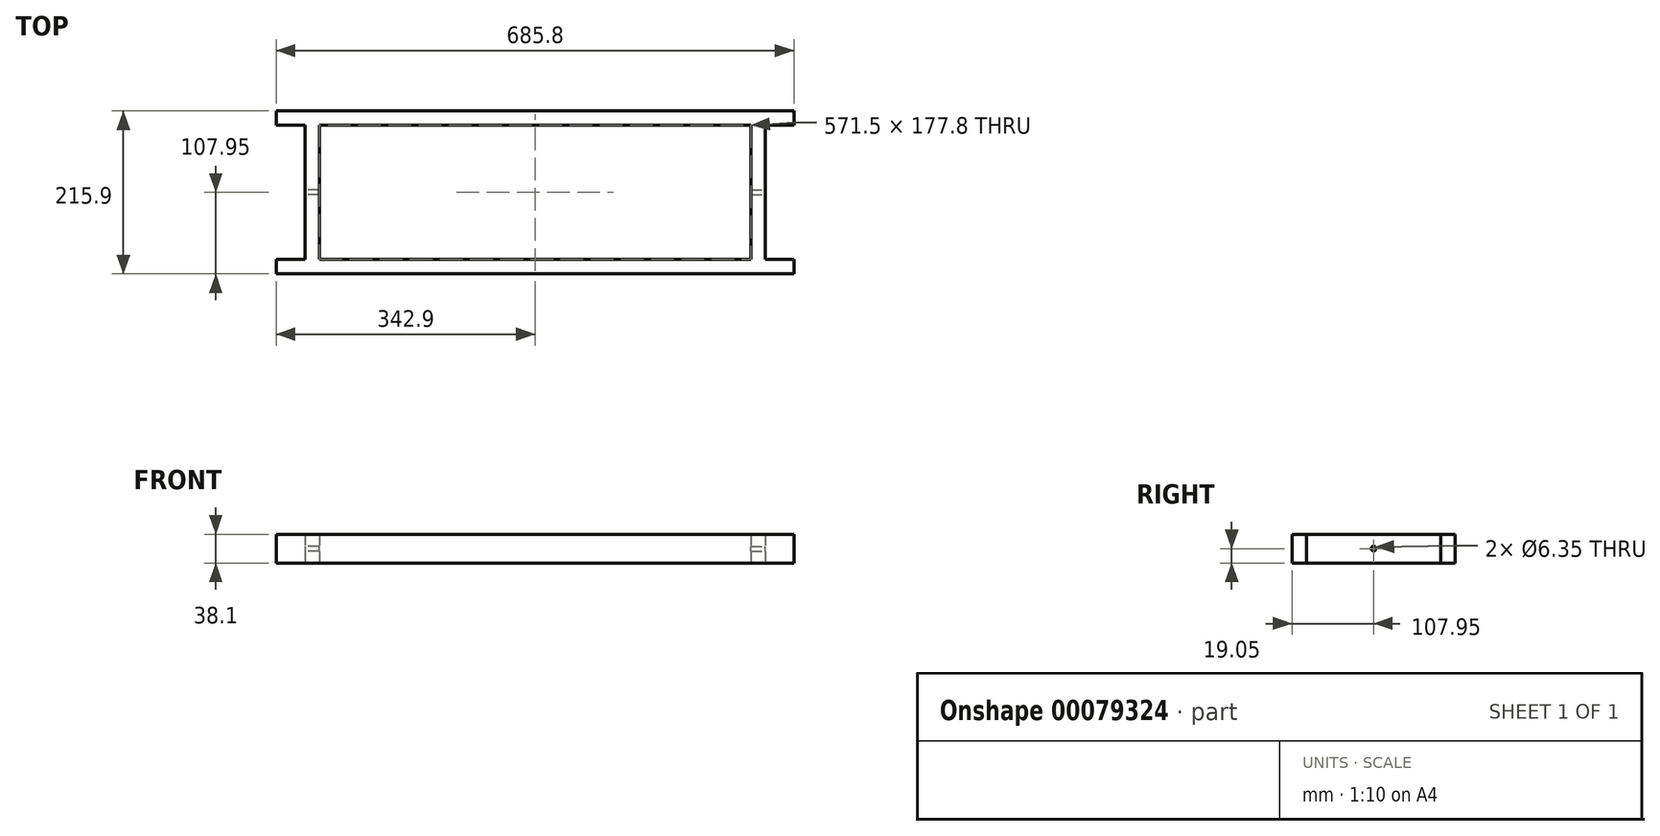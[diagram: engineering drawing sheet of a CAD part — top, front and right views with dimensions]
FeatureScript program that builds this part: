
annotation { "Feature Type Name" : "Feature", "Feature Type Description" : "" }
export const myFeature = defineFeature(function(context is Context, id is Id, definition is map)
    precondition{}
    {
        {
            var Q0;
            Q0=qCreatedBy(makeId("Top.planeOp"),FACE);
            var sketch = newSketch(context, id + "F0", { "sketchPlane" : qUnion([Q0])});
            skLineSegment(sketch, "E0.bottom", {"start": v(-342.9, 107.95) * mm, "end": v(342.9, 107.95) * mm});
            skLineSegment(sketch, "E0.top", {"start": v(-342.9, 88.9) * mm, "end": v(342.9, 88.9) * mm});
            skLineSegment(sketch, "E0.left", {"start": v(-342.9, 107.95) * mm, "end": v(-342.9, 88.9) * mm});
            skLineSegment(sketch, "E0.right", {"start": v(342.9, 107.95) * mm, "end": v(342.9, 88.9) * mm});
            skLineSegment(sketch, "E1.bottom", {"start": v(-342.9, -107.95) * mm, "end": v(342.9, -107.95) * mm});
            skLineSegment(sketch, "E1.top", {"start": v(-342.9, -88.9) * mm, "end": v(342.9, -88.9) * mm});
            skLineSegment(sketch, "E1.left", {"start": v(-342.9, -107.95) * mm, "end": v(-342.9, -88.9) * mm});
            skLineSegment(sketch, "E1.right", {"start": v(342.9, -107.95) * mm, "end": v(342.9, -88.9) * mm});
            skLineSegment(sketch, "E2.bottom", {"start": v(-304.8, 88.9) * mm, "end": v(-285.75, 88.9) * mm});
            skLineSegment(sketch, "E2.top", {"start": v(-304.8, -88.9) * mm, "end": v(-285.75, -88.9) * mm});
            skLineSegment(sketch, "E2.left", {"start": v(-304.8, 88.9) * mm, "end": v(-304.8, -88.9) * mm});
            skLineSegment(sketch, "E2.right", {"start": v(-285.75, 88.9) * mm, "end": v(-285.75, -88.9) * mm});
            skLineSegment(sketch, "E3.bottom", {"start": v(-107.95, 88.9) * mm, "end": v(-88.9, 88.9) * mm});
            skLineSegment(sketch, "E3.top", {"start": v(-107.95, -88.9) * mm, "end": v(-88.9, -88.9) * mm});
            skLineSegment(sketch, "E3.left", {"start": v(-107.95, 88.9) * mm, "end": v(-107.95, -88.9) * mm});
            skLineSegment(sketch, "E3.right", {"start": v(-88.9, 88.9) * mm, "end": v(-88.9, -88.9) * mm});
            skLineSegment(sketch, "E4.bottom", {"start": v(304.8, 88.9) * mm, "end": v(285.75, 88.9) * mm});
            skLineSegment(sketch, "E4.top", {"start": v(304.8, -88.9) * mm, "end": v(285.75, -88.9) * mm});
            skLineSegment(sketch, "E4.left", {"start": v(304.8, 88.9) * mm, "end": v(304.8, -88.9) * mm});
            skLineSegment(sketch, "E4.right", {"start": v(285.75, 88.9) * mm, "end": v(285.75, -88.9) * mm});
            skLineSegment(sketch, "E5.bottom", {"start": v(107.95, 88.9) * mm, "end": v(88.9, 88.9) * mm});
            skLineSegment(sketch, "E5.top", {"start": v(107.95, -88.9) * mm, "end": v(88.9, -88.9) * mm});
            skLineSegment(sketch, "E5.left", {"start": v(107.95, 88.9) * mm, "end": v(107.95, -88.9) * mm});
            skLineSegment(sketch, "E5.right", {"start": v(88.9, 88.9) * mm, "end": v(88.9, -88.9) * mm});
            skSolve(sketch);
        }
        {
            var Q0;
            Q0 = qSketchRegion(id + "F0", true);
            var Q1;
            Q1=makeQuery(id+"F0.imprint","IMPRINT",FACE,{"disambiguationData":[TD([[makeQuery(id+"F0.imprint","IMPRINT",EDGE,{"derivedFrom":sQuery(id+"F0.wireOp",EDGE,"E3.bottom")}),-1.0]])]});
            var Q2;
            Q2=makeQuery(id+"F0.imprint","IMPRINT",FACE,{"disambiguationData":[TD([[makeQuery(id+"F0.imprint","IMPRINT",EDGE,{"derivedFrom":sQuery(id+"F0.wireOp",EDGE,"E5.bottom")}),1.0]])]});
            extrude(context, id + "F1", {"entities" : qUnion([Q0, Q1, Q2]), "endBound" : BoundingType.SYMMETRIC, "depth" : 38.1 * mm});
        }
        {
            var Q0;
            Q0=makeQuery(id+"F1.opExtrude","SWEPT_FACE",FACE,{"disambiguationData":[OSD([sQuery(id+"F0.wireOp",EDGE,"E2.left")])]});
            var sketch = newSketch(context, id + "F2", { "sketchPlane" : qUnion([Q0])});
            skCircle(sketch, "E6", {"center": v(0, 0) * mm, "radius": 3.17 * mm});
            skSolve(sketch);
        }
        {
            var Q0;
            Q0 = qSketchRegion(id + "F2", true);
            extrude(context, id + "F3", {"entities" : qUnion([Q0]), "operationType" : NewBodyOperationType.REMOVE, "oppositeDirection" : true, "depth" : 25.4 * mm});
        }
        {
            var Q0;
            Q0=makeQuery(id+"F1.opExtrude","SWEPT_FACE",FACE,{"disambiguationData":[OSD([sQuery(id+"F0.wireOp",EDGE,"E4.left")])]});
            var sketch = newSketch(context, id + "F4", { "sketchPlane" : qUnion([Q0])});
            skCircle(sketch, "E7", {"center": v(0, 0) * mm, "radius": 3.18 * mm});
            skSolve(sketch);
        }
        {
            var Q0;
            Q0 = qSketchRegion(id + "F4", true);
            extrude(context, id + "F5", {"entities" : qUnion([Q0]), "operationType" : NewBodyOperationType.REMOVE, "oppositeDirection" : true, "depth" : 25.4 * mm});
        }
    });
